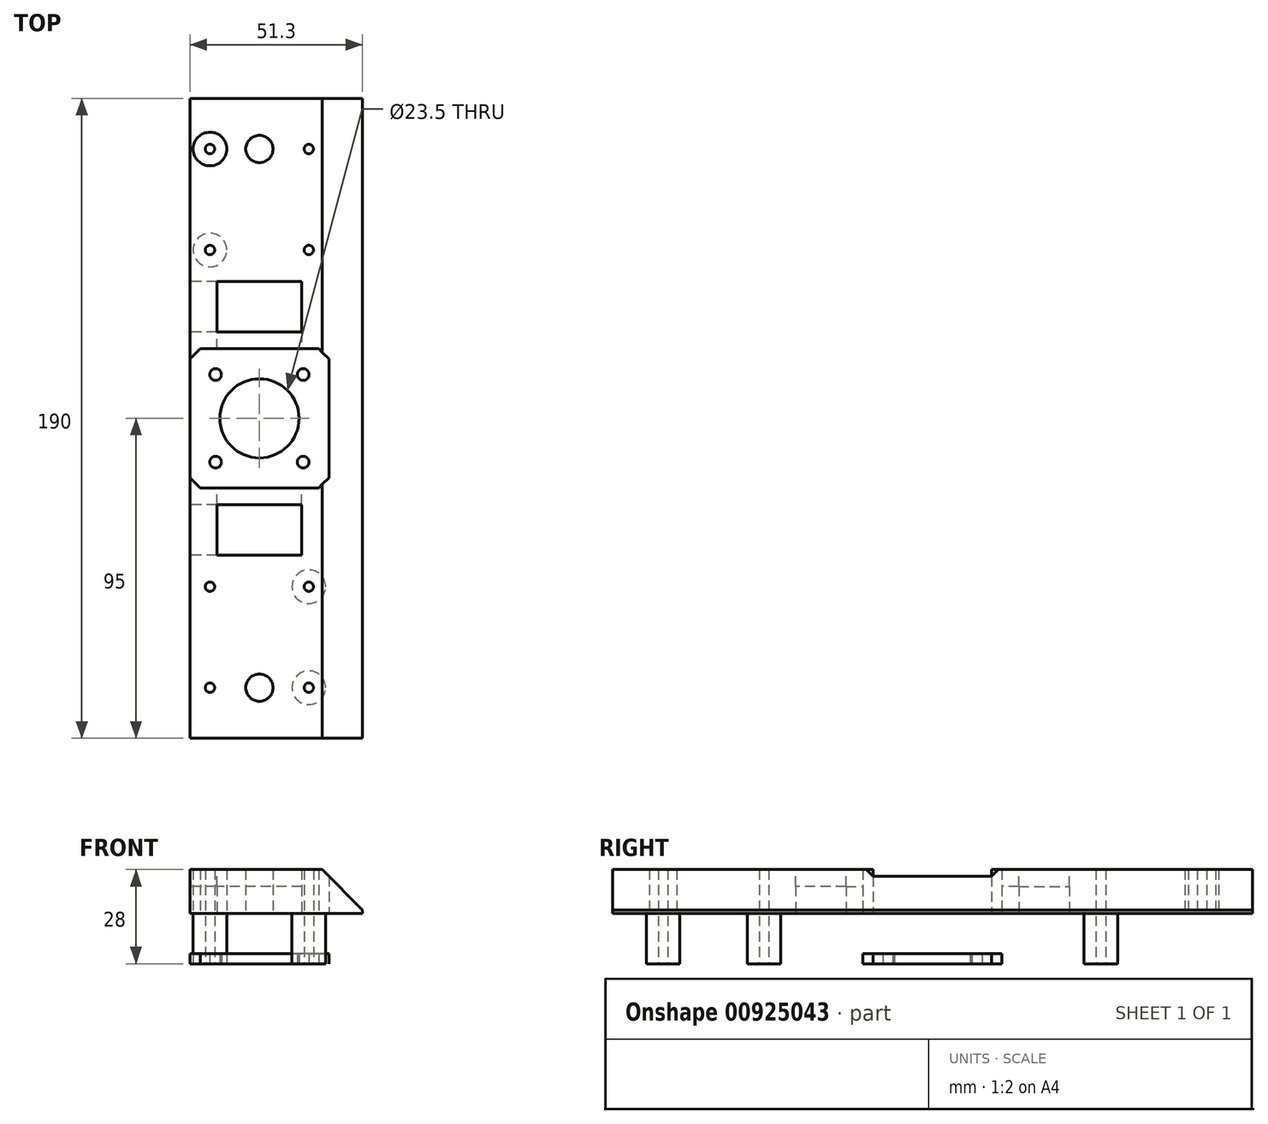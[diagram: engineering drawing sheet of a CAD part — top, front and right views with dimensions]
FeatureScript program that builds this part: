
annotation { "Feature Type Name" : "Feature", "Feature Type Description" : "" }
export const myFeature = defineFeature(function(context is Context, id is Id, definition is map)
    precondition{}
    {
        {
            var Q0;
            Q0=qCreatedBy(makeId("Top.planeOp"),FACE);
            var sketch = newSketch(context, id + "F0", { "sketchPlane" : qUnion([Q0])});
            skCircle(sketch, "E0", {"center": v(0, 0) * mm, "radius": 11.75 * mm});
            skCircle(sketch, "E1", {"center": v(13, 13) * mm, "radius": 1.75 * mm});
            skCircle(sketch, "E2.MirrorC", {"center": v(-13, -13) * mm, "radius": 1.75 * mm});
            skCircle(sketch, "E3.MirrorC", {"center": v(13, -13) * mm, "radius": 1.75 * mm});
            skLineSegment(sketch, "E4", {"start": v(-18.36, 15.65) * mm, "end": v(-15.65, 18.36) * mm});
            skLineSegment(sketch, "E5", {"start": v(-15.65, 18.36) * mm, "end": v(15.65, 18.36) * mm});
            skLineSegment(sketch, "E6", {"start": v(15.65, 18.36) * mm, "end": v(18.36, 15.65) * mm});
            skLineSegment(sketch, "E7", {"start": v(18.36, 15.65) * mm, "end": v(18.36, -15.65) * mm});
            skLineSegment(sketch, "E8", {"start": v(18.36, -15.65) * mm, "end": v(15.65, -18.36) * mm});
            skLineSegment(sketch, "E9", {"start": v(15.65, -18.36) * mm, "end": v(-15.65, -18.36) * mm});
            skLineSegment(sketch, "E10", {"start": v(-15.65, -18.36) * mm, "end": v(-18.36, -15.65) * mm});
            skLineSegment(sketch, "E11", {"start": v(-18.36, -15.65) * mm, "end": v(-18.36, 15.65) * mm});
            skCircle(sketch, "E12.MirrorC", {"center": v(-13, 13) * mm, "radius": 1.75 * mm});
            skLineSegment(sketch, "E13", {"start": v(0, 0) * mm, "end": v(-17.6, 15) * mm});
            skLineSegment(sketch, "E14", {"start": v(0, 0) * mm, "end": v(-15, 17.6) * mm});
            skLineSegment(sketch, "E15", {"start": v(0, 0) * mm, "end": v(-17.6, -15) * mm});
            skLineSegment(sketch, "E16", {"start": v(0, 0) * mm, "end": v(-15, -17.6) * mm});
            skLineSegment(sketch, "E17", {"start": v(0, 0) * mm, "end": v(15, 17.6) * mm});
            skLineSegment(sketch, "E18", {"start": v(0, 0) * mm, "end": v(17.6, 15) * mm});
            skLineSegment(sketch, "E19", {"start": v(0, 0) * mm, "end": v(15, -17.6) * mm});
            skLineSegment(sketch, "E20", {"start": v(0, 0) * mm, "end": v(17.6, -15) * mm});
            skLineSegment(sketch, "E21", {"start": v(0, 0) * mm, "end": v(15.57, 18.27) * mm});
            skLineSegment(sketch, "E22", {"start": v(0, 0) * mm, "end": v(18.27, 15.57) * mm});
            skLineSegment(sketch, "E23", {"start": v(0, 0) * mm, "end": v(18.27, -15.57) * mm});
            skLineSegment(sketch, "E24", {"start": v(0, 0) * mm, "end": v(15.57, -18.27) * mm});
            skLineSegment(sketch, "E25", {"start": v(0, 0) * mm, "end": v(-15.57, -18.27) * mm});
            skLineSegment(sketch, "E26", {"start": v(0, 0) * mm, "end": v(-18.27, -15.57) * mm});
            skLineSegment(sketch, "E27", {"start": v(0, 0) * mm, "end": v(-15.57, 18.27) * mm});
            skLineSegment(sketch, "E28", {"start": v(0, 0) * mm, "end": v(-18.27, 15.57) * mm});
            skLineSegment(sketch, "E29", {"start": v(0, 0) * mm, "end": v(17.6, 20.65) * mm});
            skLineSegment(sketch, "E30", {"start": v(17.6, 20.65) * mm, "end": v(0, 0) * mm});
            skLineSegment(sketch, "E31", {"start": v(0, 0) * mm, "end": v(20.65, 17.6) * mm});
            skLineSegment(sketch, "E32", {"start": v(0, 0) * mm, "end": v(20.65, -17.6) * mm});
            skLineSegment(sketch, "E33", {"start": v(0, 0) * mm, "end": v(17.6, -20.65) * mm});
            skLineSegment(sketch, "E34", {"start": v(0, 0) * mm, "end": v(-17.6, -20.65) * mm});
            skLineSegment(sketch, "E35", {"start": v(0, 0) * mm, "end": v(-20.65, -17.6) * mm});
            skLineSegment(sketch, "E36", {"start": v(0, 0) * mm, "end": v(-20.65, 17.6) * mm});
            skLineSegment(sketch, "E37", {"start": v(0, 0) * mm, "end": v(-17.6, 20.65) * mm});
            skLineSegment(sketch, "E38", {"start": v(17.6, 20.65) * mm, "end": v(-17.6, 20.65) * mm});
            skLineSegment(sketch, "E39", {"start": v(-17.6, 20.65) * mm, "end": v(-20.65, 17.6) * mm});
            skLineSegment(sketch, "E40", {"start": v(-20.65, 17.6) * mm, "end": v(-20.65, -17.6) * mm});
            skLineSegment(sketch, "E41", {"start": v(-20.65, -17.6) * mm, "end": v(-17.6, -20.65) * mm});
            skLineSegment(sketch, "E42", {"start": v(-17.6, -20.65) * mm, "end": v(17.6, -20.65) * mm});
            skLineSegment(sketch, "E43", {"start": v(17.6, 20.65) * mm, "end": v(20.65, 17.6) * mm});
            skLineSegment(sketch, "E44", {"start": v(20.65, 17.6) * mm, "end": v(20.65, -17.6) * mm});
            skLineSegment(sketch, "E45", {"start": v(20.65, -17.6) * mm, "end": v(17.6, -20.65) * mm});
            skLineSegment(sketch, "E46", {"start": v(20.65, 0) * mm, "end": v(30.65, 0) * mm, "construction": true});
            skLineSegment(sketch, "E47", {"start": v(30.65, 0) * mm, "end": v(30.65, -95) * mm});
            skLineSegment(sketch, "E48", {"start": v(-20.65, 0) * mm, "end": v(-20.65, -95) * mm});
            skLineSegment(sketch, "E49", {"start": v(30.65, -95) * mm, "end": v(-20.65, -95) * mm});
            skLineSegment(sketch, "E50", {"start": v(0, 0) * mm, "end": v(0, -80) * mm, "construction": true});
            skCircle(sketch, "E51", {"center": v(0, -80) * mm, "radius": 4.05 * mm});
            skLineSegment(sketch, "E52.MirrorCS", {"start": v(30.65, 0) * mm, "end": v(30.65, 95) * mm});
            skLineSegment(sketch, "E53.MirrorCS", {"start": v(-20.65, 0) * mm, "end": v(-20.65, 95) * mm});
            skLineSegment(sketch, "E54.MirrorCS", {"start": v(30.65, 95) * mm, "end": v(-20.65, 95) * mm});
            skLineSegment(sketch, "E55.MirrorCS", {"start": v(0, 0) * mm, "end": v(0, 80) * mm, "construction": true});
            skCircle(sketch, "E56.MirrorC", {"center": v(0, 80) * mm, "radius": 4.05 * mm});
            skLineSegment(sketch, "E57", {"start": v(0, -80) * mm, "end": v(-20.65, -80) * mm, "construction": true});
            skCircle(sketch, "E58", {"center": v(-14.67, -80) * mm, "radius": 1.4 * mm});
            skCircle(sketch, "E59", {"center": v(-14.67, -80) * mm, "radius": 5 * mm});
            skCircle(sketch, "E60.MirrorC", {"center": v(14.67, -80) * mm, "radius": 5 * mm});
            skCircle(sketch, "E61.MirrorC", {"center": v(14.67, -80) * mm, "radius": 1.4 * mm});
            skCircle(sketch, "E62.MirrorC", {"center": v(14.67, 80) * mm, "radius": 5 * mm});
            skCircle(sketch, "E63.MirrorC", {"center": v(14.67, 80) * mm, "radius": 1.4 * mm});
            skCircle(sketch, "E64.MirrorC", {"center": v(-14.67, 80) * mm, "radius": 1.4 * mm});
            skCircle(sketch, "E65.MirrorC", {"center": v(-14.67, 80) * mm, "radius": 5 * mm});
            skCircle(sketch, "E66.0.1.0", {"center": v(14.67, -50) * mm, "radius": 5 * mm});
            skLineSegment(sketch, "E66.direction2", {"start": v(14.67, -80) * mm, "end": v(14.67, -50) * mm, "construction": true});
            skCircle(sketch, "E67.0.1.0", {"center": v(14.67, -50) * mm, "radius": 1.4 * mm});
            skCircle(sketch, "E68.MirrorC", {"center": v(-14.67, -50) * mm, "radius": 5 * mm});
            skCircle(sketch, "E69", {"center": v(-14.67, -50) * mm, "radius": 1.4 * mm});
            skCircle(sketch, "E70.MirrorC", {"center": v(-14.67, 50) * mm, "radius": 5 * mm});
            skCircle(sketch, "E71.MirrorC", {"center": v(-14.67, 50) * mm, "radius": 1.4 * mm});
            skLineSegment(sketch, "E72", {"start": v(14.67, 80) * mm, "end": v(14.67, 50) * mm, "construction": true});
            skCircle(sketch, "E73", {"center": v(14.67, 50) * mm, "radius": 5 * mm});
            skCircle(sketch, "E74", {"center": v(14.67, 50) * mm, "radius": 1.4 * mm});
            skLineSegment(sketch, "E75", {"start": v(-14.67, 80) * mm, "end": v(-14.67, 50) * mm, "construction": true});
            skSolve(sketch);
        }
        {
            var Q0;
            Q0=makeQuery(id+"F0.imprint","IMPRINT",FACE,{"disambiguationData":[TD([[makeQuery(id+"F0.imprint","IMPRINT",EDGE,{"derivedFrom":sQuery(id+"F0.wireOp",EDGE,"E38")}),-1.0]])]});
            var Q1;
            Q1=makeQuery(id+"F0.imprint","IMPRINT",FACE,{"disambiguationData":[TD([[makeQuery(id+"F0.imprint","IMPRINT",EDGE,{"derivedFrom":sQuery(id+"F0.wireOp",EDGE,"E58")}),-1.0]])]});
            var Q2;
            Q2=makeQuery(id+"F0.imprint","IMPRINT",FACE,{"disambiguationData":[TD([[makeQuery(id+"F0.imprint","IMPRINT",EDGE,{"derivedFrom":sQuery(id+"F0.wireOp",EDGE,"E58")}),1.0]])]});
            var Q3;
            Q3=makeQuery(id+"F0.imprint","IMPRINT",FACE,{"disambiguationData":[TD([[makeQuery(id+"F0.imprint","IMPRINT",EDGE,{"derivedFrom":sQuery(id+"F0.wireOp",EDGE,"E60.MirrorC")}),-1.0]])]});
            var Q4;
            Q4=makeQuery(id+"F0.imprint","IMPRINT",FACE,{"disambiguationData":[TD([[makeQuery(id+"F0.imprint","IMPRINT",EDGE,{"derivedFrom":sQuery(id+"F0.wireOp",EDGE,"E61.MirrorC")}),-1.0]])]});
            var Q5;
            Q5=makeQuery(id+"F0.imprint","IMPRINT",FACE,{"disambiguationData":[TD([[makeQuery(id+"F0.imprint","IMPRINT",EDGE,{"derivedFrom":sQuery(id+"F0.wireOp",EDGE,"E62.MirrorC")}),1.0]])]});
            var Q6;
            Q6=makeQuery(id+"F0.imprint","IMPRINT",FACE,{"disambiguationData":[TD([[makeQuery(id+"F0.imprint","IMPRINT",EDGE,{"derivedFrom":sQuery(id+"F0.wireOp",EDGE,"E63.MirrorC")}),1.0]])]});
            var Q7;
            Q7=makeQuery(id+"F0.imprint","IMPRINT",FACE,{"disambiguationData":[TD([[makeQuery(id+"F0.imprint","IMPRINT",EDGE,{"derivedFrom":sQuery(id+"F0.wireOp",EDGE,"E64.MirrorC")}),1.0]])]});
            var Q8;
            Q8=makeQuery(id+"F0.imprint","IMPRINT",FACE,{"disambiguationData":[TD([[makeQuery(id+"F0.imprint","IMPRINT",EDGE,{"derivedFrom":sQuery(id+"F0.wireOp",EDGE,"E64.MirrorC")}),-1.0]])]});
            var Q9;
            Q9=makeQuery(id+"F0.imprint","IMPRINT",FACE,{"disambiguationData":[TD([[makeQuery(id+"F0.imprint","IMPRINT",EDGE,{"derivedFrom":sQuery(id+"F0.wireOp",EDGE,"E66.0.1.0")}),-1.0]])]});
            var Q10;
            Q10=makeQuery(id+"F0.imprint","IMPRINT",FACE,{"disambiguationData":[TD([[makeQuery(id+"F0.imprint","IMPRINT",EDGE,{"derivedFrom":sQuery(id+"F0.wireOp",EDGE,"E67.0.1.0")}),-1.0]])]});
            var Q11;
            Q11=makeQuery(id+"F0.imprint","IMPRINT",FACE,{"disambiguationData":[TD([[makeQuery(id+"F0.imprint","IMPRINT",EDGE,{"derivedFrom":sQuery(id+"F0.wireOp",EDGE,"E68.MirrorC")}),1.0]])]});
            var Q12;
            Q12=makeQuery(id+"F0.imprint","IMPRINT",FACE,{"disambiguationData":[TD([[makeQuery(id+"F0.imprint","IMPRINT",EDGE,{"derivedFrom":sQuery(id+"F0.wireOp",EDGE,"E73")}),1.0]])]});
            var Q13;
            Q13=makeQuery(id+"F0.imprint","IMPRINT",FACE,{"disambiguationData":[TD([[makeQuery(id+"F0.imprint","IMPRINT",EDGE,{"derivedFrom":sQuery(id+"F0.wireOp",EDGE,"E74")}),1.0]])]});
            var Q14;
            Q14=makeQuery(id+"F0.imprint","IMPRINT",FACE,{"disambiguationData":[TD([[makeQuery(id+"F0.imprint","IMPRINT",EDGE,{"derivedFrom":sQuery(id+"F0.wireOp",EDGE,"E70.MirrorC")}),-1.0]])]});
            var Q15;
            Q15=makeQuery(id+"F0.imprint","IMPRINT",FACE,{"disambiguationData":[TD([[makeQuery(id+"F0.imprint","IMPRINT",EDGE,{"derivedFrom":sQuery(id+"F0.wireOp",EDGE,"E71.MirrorC")}),-1.0]])]});
            var Q16;
            Q16=makeQuery(id+"F0.imprint","IMPRINT",FACE,{"disambiguationData":[TD([[makeQuery(id+"F0.imprint","IMPRINT",EDGE,{"derivedFrom":sQuery(id+"F0.wireOp",EDGE,"E69")}),1.0]])]});
            extrude(context, id + "F1", {"entities" : qUnion([Q0, Q1, Q2, Q3, Q4, Q5, Q6, Q7, Q8, Q9, Q10, Q11, Q12, Q13, Q14, Q15, Q16]), "depth" : 28 * mm, "offsetDistance" : 25 * mm});
        }
        {
            var Q0;
            {var subQ0=sQuery(id+"F0.wireOp",EDGE,"E9");Q0=makeQuery(id+"F0.imprint","IMPRINT",FACE,{"disambiguationData":[TD([[makeQuery(id+"F0.imprint","IMPRINT",EDGE,{"derivedFrom":subQ0}),1.0]])]});}
            var Q1;
            {var subQ0=sQuery(id+"F0.wireOp",EDGE,"E10");Q1=makeQuery(id+"F0.imprint","IMPRINT",FACE,{"disambiguationData":[TD([[makeQuery(id+"F0.imprint","IMPRINT",EDGE,{"derivedFrom":subQ0}),1.0]])]});}
            var Q2;
            {var subQ6=sQuery(id+"F0.wireOp",EDGE,"E11");Q2=makeQuery(id+"F0.imprint","IMPRINT",FACE,{"disambiguationData":[TD([[makeQuery(id+"F0.imprint","IMPRINT",EDGE,{"derivedFrom":subQ6}),1.0]])]});}
            var Q3;
            {var subQ0=sQuery(id+"F0.wireOp",EDGE,"E4");Q3=makeQuery(id+"F0.imprint","IMPRINT",FACE,{"disambiguationData":[TD([[makeQuery(id+"F0.imprint","IMPRINT",EDGE,{"derivedFrom":subQ0}),1.0]])]});}
            var Q4;
            {var subQ0=sQuery(id+"F0.wireOp",EDGE,"E5");Q4=makeQuery(id+"F0.imprint","IMPRINT",FACE,{"disambiguationData":[TD([[makeQuery(id+"F0.imprint","IMPRINT",EDGE,{"derivedFrom":subQ0}),1.0]])]});}
            var Q5;
            {var subQ0=sQuery(id+"F0.wireOp",EDGE,"E6");Q5=makeQuery(id+"F0.imprint","IMPRINT",FACE,{"disambiguationData":[TD([[makeQuery(id+"F0.imprint","IMPRINT",EDGE,{"derivedFrom":subQ0}),1.0]])]});}
            var Q6;
            {var subQ0=sQuery(id+"F0.wireOp",EDGE,"E7");Q6=makeQuery(id+"F0.imprint","IMPRINT",FACE,{"disambiguationData":[TD([[makeQuery(id+"F0.imprint","IMPRINT",EDGE,{"derivedFrom":subQ0}),1.0]])]});}
            var Q7;
            {var subQ0=sQuery(id+"F0.wireOp",EDGE,"E8");Q7=makeQuery(id+"F0.imprint","IMPRINT",FACE,{"disambiguationData":[TD([[makeQuery(id+"F0.imprint","IMPRINT",EDGE,{"derivedFrom":subQ0}),1.0]])]});}
            var Q8;
            {var subQ8=sQuery(id+"F0.wireOp",EDGE,"E7");Q8=makeQuery(id+"F0.imprint","IMPRINT",FACE,{"disambiguationData":[TD([[makeQuery(id+"F0.imprint","IMPRINT",EDGE,{"derivedFrom":subQ8}),-1.0]])]});}
            var Q9;
            {var subQ0=sQuery(id+"F0.wireOp",EDGE,"E33");var subQ1=sQuery(id+"F0.wireOp",EDGE,"E0");var subQ2=makeQuery(id+"F0.imprint","INTERSECT",VERTEX,{"derivedFrom":[subQ1,subQ0]});Q9=makeQuery(id+"F0.imprint","IMPRINT",FACE,{"disambiguationData":[TD([[makeQuery(id+"F0.imprint","IMPRINT",EDGE,{"disambiguationData":[TD([[subQ2,-1.0]])],"derivedFrom":subQ1}),-1.0]])]});}
            var Q10;
            {var subQ5=sQuery(id+"F0.wireOp",EDGE,"E8");Q10=makeQuery(id+"F0.imprint","IMPRINT",FACE,{"disambiguationData":[TD([[makeQuery(id+"F0.imprint","IMPRINT",EDGE,{"derivedFrom":subQ5}),-1.0]])]});}
            var Q11;
            {var subQ13=sQuery(id+"F0.wireOp",EDGE,"E9");Q11=makeQuery(id+"F0.imprint","IMPRINT",FACE,{"disambiguationData":[TD([[makeQuery(id+"F0.imprint","IMPRINT",EDGE,{"derivedFrom":subQ13}),-1.0]])]});}
            var Q12;
            {var subQ5=sQuery(id+"F0.wireOp",EDGE,"E10");Q12=makeQuery(id+"F0.imprint","IMPRINT",FACE,{"disambiguationData":[TD([[makeQuery(id+"F0.imprint","IMPRINT",EDGE,{"derivedFrom":subQ5}),-1.0]])]});}
            var Q13;
            {var subQ0=sQuery(id+"F0.wireOp",EDGE,"E35");var subQ1=sQuery(id+"F0.wireOp",EDGE,"E0");var subQ2=makeQuery(id+"F0.imprint","INTERSECT",VERTEX,{"derivedFrom":[subQ1,subQ0]});Q13=makeQuery(id+"F0.imprint","IMPRINT",FACE,{"disambiguationData":[TD([[makeQuery(id+"F0.imprint","IMPRINT",EDGE,{"disambiguationData":[TD([[subQ2,-1.0]])],"derivedFrom":subQ1}),-1.0]])]});}
            var Q14;
            {var subQ8=sQuery(id+"F0.wireOp",EDGE,"E11");Q14=makeQuery(id+"F0.imprint","IMPRINT",FACE,{"disambiguationData":[TD([[makeQuery(id+"F0.imprint","IMPRINT",EDGE,{"derivedFrom":subQ8}),-1.0]])]});}
            var Q15;
            {var subQ0=sQuery(id+"F0.wireOp",EDGE,"E37");var subQ1=sQuery(id+"F0.wireOp",EDGE,"E0");var subQ2=makeQuery(id+"F0.imprint","INTERSECT",VERTEX,{"derivedFrom":[subQ1,subQ0]});Q15=makeQuery(id+"F0.imprint","IMPRINT",FACE,{"disambiguationData":[TD([[makeQuery(id+"F0.imprint","IMPRINT",EDGE,{"disambiguationData":[TD([[subQ2,-1.0]])],"derivedFrom":subQ1}),-1.0]])]});}
            var Q16;
            {var subQ7=sQuery(id+"F0.wireOp",EDGE,"E4");Q16=makeQuery(id+"F0.imprint","IMPRINT",FACE,{"disambiguationData":[TD([[makeQuery(id+"F0.imprint","IMPRINT",EDGE,{"derivedFrom":subQ7}),-1.0]])]});}
            var Q17;
            {var subQ13=sQuery(id+"F0.wireOp",EDGE,"E5");Q17=makeQuery(id+"F0.imprint","IMPRINT",FACE,{"disambiguationData":[TD([[makeQuery(id+"F0.imprint","IMPRINT",EDGE,{"derivedFrom":subQ13}),-1.0]])]});}
            var Q18;
            {var subQ0=sQuery(id+"F0.wireOp",EDGE,"E30");var subQ1=sQuery(id+"F0.wireOp",EDGE,"E0");var subQ2=makeQuery(id+"F0.imprint","INTERSECT",VERTEX,{"derivedFrom":[subQ1,subQ0]});Q18=makeQuery(id+"F0.imprint","IMPRINT",FACE,{"disambiguationData":[TD([[makeQuery(id+"F0.imprint","IMPRINT",EDGE,{"disambiguationData":[TD([[subQ2,1.0]])],"derivedFrom":subQ1}),-1.0]])]});}
            var Q19;
            {var subQ3=sQuery(id+"F0.wireOp",EDGE,"E6");Q19=makeQuery(id+"F0.imprint","IMPRINT",FACE,{"disambiguationData":[TD([[makeQuery(id+"F0.imprint","IMPRINT",EDGE,{"derivedFrom":subQ3}),-1.0]])]});}
            extrude(context, id + "F2", {"entities" : qUnion([Q0, Q1, Q2, Q3, Q4, Q5, Q6, Q7, Q8, Q9, Q10, Q11, Q12, Q13, Q14, Q15, Q16, Q17, Q18, Q19]), "operationType" : NewBodyOperationType.ADD, "depth" : 3 * mm, "offsetDistance" : 25 * mm});
        }
        {
            var Q0;
            Q0=makeQuery(id+"F1.opExtrude","CAP_EDGE",EDGE,{"disambiguationData":[OSD([sQuery(id+"F0.wireOp",EDGE,"E47"),sQuery(id+"F0.wireOp",EDGE,"E52.MirrorCS")])],"isStart":false});
            chamfer(context, id + "F3", {"entities" : qUnion([Q0]), "width" : 12 * mm, "tangentPropagation" : true});
        }
        {
            var Q0;
            Q0=makeQuery(id+"F1.opExtrude","SWEPT_FACE",FACE,{"disambiguationData":[OSD([sQuery(id+"F0.wireOp",EDGE,"E42")])]});
            var sketch = newSketch(context, id + "F4", { "sketchPlane" : qUnion([Q0])});
            skLineSegment(sketch, "E76", {"start": v(17.6, 15.5) * mm, "end": v(12.6, 15.5) * mm});
            skLineSegment(sketch, "E77", {"start": v(0, 28) * mm, "end": v(0, 23) * mm});
            skLineSegment(sketch, "E78.bottom", {"start": v(12.6, 23) * mm, "end": v(0, 23) * mm});
            skLineSegment(sketch, "E78.top", {"start": v(12.6, 15.5) * mm, "end": v(0, 15.5) * mm});
            skLineSegment(sketch, "E78.left", {"start": v(12.6, 23) * mm, "end": v(12.6, 15.5) * mm});
            skLineSegment(sketch, "E78.right", {"start": v(0, 23) * mm, "end": v(0, 15.5) * mm});
            skLineSegment(sketch, "E79.MirrorCS", {"start": v(12.6, 8) * mm, "end": v(12.6, 15.5) * mm});
            skLineSegment(sketch, "E80.MirrorCS", {"start": v(12.6, 8) * mm, "end": v(0, 8) * mm});
            skLineSegment(sketch, "E81.MirrorCS", {"start": v(-12.6, 23) * mm, "end": v(0, 23) * mm});
            skLineSegment(sketch, "E82.MirrorCS", {"start": v(-12.6, 23) * mm, "end": v(-12.6, 15.5) * mm});
            skLineSegment(sketch, "E83.MirrorCS", {"start": v(-12.6, 8) * mm, "end": v(-12.6, 15.5) * mm});
            skLineSegment(sketch, "E84.MirrorCS", {"start": v(-12.6, 8) * mm, "end": v(0, 8) * mm});
            skSolve(sketch);
        }
        {
            var Q0;
            Q0=makeQuery(id+"F4.imprint","IMPRINT",FACE,{"disambiguationData":[TD([[makeQuery(id+"F4.imprint","IMPRINT",EDGE,{"derivedFrom":sQuery(id+"F4.wireOp",EDGE,"E78.top")}),1.0]])]});
            var Q1;
            Q1=makeQuery(id+"F4.imprint","IMPRINT",FACE,{"disambiguationData":[TD([[makeQuery(id+"F4.imprint","IMPRINT",EDGE,{"derivedFrom":sQuery(id+"F4.wireOp",EDGE,"E78.bottom")}),1.0]])]});
            extrude(context, id + "F5", {"entities" : qUnion([Q0, Q1]), "operationType" : NewBodyOperationType.REMOVE, "oppositeDirection" : true, "depth" : 20 * mm, "offsetDistance" : 25 * mm});
        }
        {
            var Q0;
            Q0=makeQuery(id+"F1.opExtrude","SWEPT_FACE",FACE,{"disambiguationData":[OSD([sQuery(id+"F0.wireOp",EDGE,"E38")])]});
            var sketch = newSketch(context, id + "F6", { "sketchPlane" : qUnion([Q0])});
            skLineSegment(sketch, "E85", {"start": v(0, 3) * mm, "end": v(0, 8) * mm});
            skLineSegment(sketch, "E86", {"start": v(-17.6, 15.5) * mm, "end": v(-12.6, 15.5) * mm});
            skLineSegment(sketch, "E87.bottom", {"start": v(-12.6, 15.5) * mm, "end": v(0, 15.5) * mm});
            skLineSegment(sketch, "E87.top", {"start": v(-12.6, 8) * mm, "end": v(0, 8) * mm});
            skLineSegment(sketch, "E87.left", {"start": v(-12.6, 15.5) * mm, "end": v(-12.6, 8) * mm});
            skLineSegment(sketch, "E87.right", {"start": v(0, 15.5) * mm, "end": v(0, 8) * mm});
            skLineSegment(sketch, "E88.MirrorCS", {"start": v(12.6, 8) * mm, "end": v(0, 8) * mm});
            skLineSegment(sketch, "E89.MirrorCS", {"start": v(12.6, 15.5) * mm, "end": v(0, 15.5) * mm});
            skLineSegment(sketch, "E90.MirrorCS", {"start": v(12.6, 15.5) * mm, "end": v(12.6, 8) * mm});
            skLineSegment(sketch, "E91.MirrorCS", {"start": v(12.6, 23) * mm, "end": v(0, 23) * mm});
            skLineSegment(sketch, "E92.MirrorCS", {"start": v(12.6, 15.5) * mm, "end": v(12.6, 23) * mm});
            skLineSegment(sketch, "E93.MirrorCS", {"start": v(-12.6, 23) * mm, "end": v(0, 23) * mm});
            skLineSegment(sketch, "E94.MirrorCS", {"start": v(-12.6, 15.5) * mm, "end": v(-12.6, 23) * mm});
            skSolve(sketch);
        }
        {
            var Q0;
            Q0=makeQuery(id+"F6.imprint","IMPRINT",FACE,{"disambiguationData":[TD([[makeQuery(id+"F6.imprint","IMPRINT",EDGE,{"derivedFrom":sQuery(id+"F6.wireOp",EDGE,"E87.right")}),1.0]])]});
            var Q1;
            Q1=makeQuery(id+"F6.imprint","IMPRINT",FACE,{"disambiguationData":[TD([[makeQuery(id+"F6.imprint","IMPRINT",EDGE,{"derivedFrom":sQuery(id+"F6.wireOp",EDGE,"E87.top")}),1.0]])]});
            var Q2;
            Q2=makeQuery(id+"F6.imprint","IMPRINT",FACE,{"disambiguationData":[TD([[makeQuery(id+"F6.imprint","IMPRINT",EDGE,{"derivedFrom":sQuery(id+"F6.wireOp",EDGE,"E89.MirrorCS")}),-1.0]])]});
            extrude(context, id + "F7", {"entities" : qUnion([Q0, Q1, Q2]), "operationType" : NewBodyOperationType.REMOVE, "oppositeDirection" : true, "depth" : 20 * mm, "offsetDistance" : 25 * mm});
        }
        {
            var Q0;
            Q0=makeQuery(id+"F3.opChamfer","SPLIT",FACE,{"disambiguationData":[OD(0.0)],"derivedFrom":makeQuery(id+"F1.opExtrude","CAP_FACE",FACE,{"disambiguationData":[OSD([sQuery(id+"F0.wireOp",EDGE,"E38"),sQuery(id+"F0.wireOp",EDGE,"E39"),sQuery(id+"F0.wireOp",EDGE,"E41"),sQuery(id+"F0.wireOp",EDGE,"E42"),sQuery(id+"F0.wireOp",EDGE,"E43"),sQuery(id+"F0.wireOp",EDGE,"E44"),sQuery(id+"F0.wireOp",EDGE,"E45"),sQuery(id+"F0.wireOp",EDGE,"E47"),sQuery(id+"F0.wireOp",EDGE,"E48"),sQuery(id+"F0.wireOp",EDGE,"E49"),sQuery(id+"F0.wireOp",EDGE,"E51"),sQuery(id+"F0.wireOp",EDGE,"E52.MirrorCS"),sQuery(id+"F0.wireOp",EDGE,"E53.MirrorCS"),sQuery(id+"F0.wireOp",EDGE,"E54.MirrorCS"),sQuery(id+"F0.wireOp",EDGE,"E56.MirrorC")])],"isStart":false})});
            var sketch = newSketch(context, id + "F8", { "sketchPlane" : qUnion([Q0])});
            skLineSegment(sketch, "E95", {"start": v(0, 20.65) * mm, "end": v(0, 40.65) * mm, "construction": true});
            skLineSegment(sketch, "E96.bottom", {"start": v(0, 40.65) * mm, "end": v(12.59, 40.65) * mm});
            skLineSegment(sketch, "E96.top", {"start": v(0, 25.65) * mm, "end": v(12.59, 25.65) * mm});
            skLineSegment(sketch, "E96.left", {"start": v(0, 40.65) * mm, "end": v(0, 25.65) * mm});
            skLineSegment(sketch, "E96.right", {"start": v(12.59, 40.65) * mm, "end": v(12.59, 25.65) * mm});
            skLineSegment(sketch, "E97.MirrorCS", {"start": v(0, 40.65) * mm, "end": v(-12.6, 40.65) * mm});
            skLineSegment(sketch, "E98.MirrorCS", {"start": v(-12.6, 40.65) * mm, "end": v(-12.6, 25.65) * mm});
            skLineSegment(sketch, "E99.MirrorCS", {"start": v(0, 25.65) * mm, "end": v(-12.6, 25.65) * mm});
            skLineSegment(sketch, "E100", {"start": v(-12.6, 25.65) * mm, "end": v(-20.65, 25.65) * mm, "construction": true});
            skSolve(sketch);
        }
        {
            var Q0;
            Q0=makeQuery(id+"F8.imprint","IMPRINT",FACE,{"disambiguationData":[TD([[makeQuery(id+"F8.imprint","IMPRINT",EDGE,{"derivedFrom":sQuery(id+"F8.wireOp",EDGE,"E96.bottom")}),-1.0]])]});
            var Q1;
            Q1=makeQuery(id+"F8.imprint","IMPRINT",FACE,{"disambiguationData":[TD([[makeQuery(id+"F8.imprint","IMPRINT",EDGE,{"derivedFrom":sQuery(id+"F8.wireOp",EDGE,"E96.left")}),-1.0]])]});
            extrude(context, id + "F9", {"entities" : qUnion([Q0, Q1]), "operationType" : NewBodyOperationType.REMOVE, "oppositeDirection" : true, "depth" : 28 * mm, "offsetDistance" : 25 * mm});
        }
        {
            var Q0;
            {var subQ0=sQuery(id+"F0.wireOp",EDGE,"E53.MirrorCS");var subQ1=sQuery(id+"F0.wireOp",EDGE,"E48");Q0=makeQuery(id+"F2.boolean.opBoolean","MERGE",FACE,{"derivedFrom":[makeQuery(id+"F1.opExtrude","SWEPT_FACE",FACE,{"disambiguationData":[OSD([subQ1])]}),makeQuery(id+"F1.opExtrude","SWEPT_FACE",FACE,{"disambiguationData":[OSD([subQ0])]}),makeQuery(id+"F2.opExtrude","SWEPT_FACE",FACE,{"disambiguationData":[OSD([subQ1,subQ0])]})]});}
            var sketch = newSketch(context, id + "F10", { "sketchPlane" : qUnion([Q0])});
            skLineSegment(sketch, "E101", {"start": v(-25.65, 28) * mm, "end": v(-25.65, 23) * mm});
            skLineSegment(sketch, "E102.bottom", {"start": v(-25.65, 23) * mm, "end": v(-40.65, 23) * mm});
            skLineSegment(sketch, "E102.top", {"start": v(-25.65, 3) * mm, "end": v(-40.65, 3) * mm});
            skLineSegment(sketch, "E102.left", {"start": v(-25.65, 23) * mm, "end": v(-25.65, 3) * mm});
            skLineSegment(sketch, "E102.right", {"start": v(-40.65, 23) * mm, "end": v(-40.65, 3) * mm});
            skLineSegment(sketch, "E103.MirrorCS", {"start": v(25.65, 3) * mm, "end": v(40.65, 3) * mm});
            skLineSegment(sketch, "E104.MirrorCS", {"start": v(40.65, 23) * mm, "end": v(40.65, 3) * mm});
            skLineSegment(sketch, "E105.MirrorCS", {"start": v(25.65, 23) * mm, "end": v(40.65, 23) * mm});
            skLineSegment(sketch, "E106.MirrorCS", {"start": v(25.65, 23) * mm, "end": v(25.65, 3) * mm});
            skSolve(sketch);
        }
        {
            var Q0;
            Q0=makeQuery(id+"F10.imprint","IMPRINT",FACE,{"disambiguationData":[TD([[makeQuery(id+"F10.imprint","IMPRINT",EDGE,{"derivedFrom":sQuery(id+"F10.wireOp",EDGE,"E102.bottom")}),1.0]])]});
            extrude(context, id + "F11", {"entities" : qUnion([Q0]), "operationType" : NewBodyOperationType.REMOVE, "oppositeDirection" : true, "depth" : 25 * mm, "offsetDistance" : 25 * mm});
        }
        {
            var Q0;
            Q0=makeQuery(id+"F3.opChamfer","SPLIT",FACE,{"disambiguationData":[OD(1.0)],"derivedFrom":makeQuery(id+"F1.opExtrude","CAP_FACE",FACE,{"disambiguationData":[OSD([sQuery(id+"F0.wireOp",EDGE,"E38"),sQuery(id+"F0.wireOp",EDGE,"E39"),sQuery(id+"F0.wireOp",EDGE,"E41"),sQuery(id+"F0.wireOp",EDGE,"E42"),sQuery(id+"F0.wireOp",EDGE,"E43"),sQuery(id+"F0.wireOp",EDGE,"E44"),sQuery(id+"F0.wireOp",EDGE,"E45"),sQuery(id+"F0.wireOp",EDGE,"E47"),sQuery(id+"F0.wireOp",EDGE,"E48"),sQuery(id+"F0.wireOp",EDGE,"E49"),sQuery(id+"F0.wireOp",EDGE,"E51"),sQuery(id+"F0.wireOp",EDGE,"E52.MirrorCS"),sQuery(id+"F0.wireOp",EDGE,"E53.MirrorCS"),sQuery(id+"F0.wireOp",EDGE,"E54.MirrorCS"),sQuery(id+"F0.wireOp",EDGE,"E56.MirrorC")])],"isStart":false})});
            var sketch = newSketch(context, id + "F12", { "sketchPlane" : qUnion([Q0])});
            skLineSegment(sketch, "E107", {"start": v(0, -20.65) * mm, "end": v(0, -40.65) * mm, "construction": true});
            skLineSegment(sketch, "E108.bottom", {"start": v(0, -40.65) * mm, "end": v(-12.59, -40.65) * mm});
            skLineSegment(sketch, "E108.top", {"start": v(0, -25.65) * mm, "end": v(-12.59, -25.65) * mm});
            skLineSegment(sketch, "E108.left", {"start": v(1.85, 8.61) * mm, "end": v(1.85, -6.39) * mm});
            skLineSegment(sketch, "E108.right", {"start": v(-12.59, -40.65) * mm, "end": v(-12.59, -25.65) * mm});
            skLineSegment(sketch, "E109.MirrorCS", {"start": v(0, -40.65) * mm, "end": v(12.6, -40.65) * mm});
            skLineSegment(sketch, "E110.MirrorCS", {"start": v(12.6, -40.65) * mm, "end": v(12.6, -25.65) * mm});
            skLineSegment(sketch, "E111.MirrorCS", {"start": v(0, -25.65) * mm, "end": v(12.6, -25.65) * mm});
            skLineSegment(sketch, "E112", {"start": v(-10.74, -6.39) * mm, "end": v(-18.8, -6.39) * mm, "construction": true});
            skSolve(sketch);
        }
        {
            var Q0;
            Q0=makeQuery(id+"F12.imprint","IMPRINT",FACE,{"disambiguationData":[TD([[makeQuery(id+"F12.imprint","IMPRINT",EDGE,{"derivedFrom":sQuery(id+"F12.wireOp",EDGE,"E108.bottom")}),-1.0]])]});
            extrude(context, id + "F13", {"entities" : qUnion([Q0]), "operationType" : NewBodyOperationType.REMOVE, "oppositeDirection" : true, "depth" : 28 * mm, "offsetDistance" : 25 * mm});
        }
        {
            var Q0;
            Q0=makeQuery(id+"F10.imprint","IMPRINT",FACE,{"disambiguationData":[TD([[makeQuery(id+"F10.imprint","IMPRINT",EDGE,{"derivedFrom":sQuery(id+"F10.wireOp",EDGE,"E103.MirrorCS")}),1.0]])]});
            extrude(context, id + "F14", {"entities" : qUnion([Q0]), "operationType" : NewBodyOperationType.REMOVE, "oppositeDirection" : true, "depth" : 25 * mm, "offsetDistance" : 25 * mm});
        }
        {
            var Q0;
            Q0=makeQuery(id+"F0.imprint","IMPRINT",FACE,{"disambiguationData":[TD([[makeQuery(id+"F0.imprint","IMPRINT",EDGE,{"derivedFrom":sQuery(id+"F0.wireOp",EDGE,"E60.MirrorC")}),-1.0]])]});
            var Q1;
            Q1=makeQuery(id+"F0.imprint","IMPRINT",FACE,{"disambiguationData":[TD([[makeQuery(id+"F0.imprint","IMPRINT",EDGE,{"derivedFrom":sQuery(id+"F0.wireOp",EDGE,"E58")}),-1.0]])]});
            var Q2;
            Q2=makeQuery(id+"F0.imprint","IMPRINT",FACE,{"disambiguationData":[TD([[makeQuery(id+"F0.imprint","IMPRINT",EDGE,{"derivedFrom":sQuery(id+"F0.wireOp",EDGE,"E68.MirrorC")}),1.0]])]});
            var Q3;
            Q3=makeQuery(id+"F0.imprint","IMPRINT",FACE,{"disambiguationData":[TD([[makeQuery(id+"F0.imprint","IMPRINT",EDGE,{"derivedFrom":sQuery(id+"F0.wireOp",EDGE,"E66.0.1.0")}),-1.0]])]});
            var Q4;
            Q4=makeQuery(id+"F0.imprint","IMPRINT",FACE,{"disambiguationData":[TD([[makeQuery(id+"F0.imprint","IMPRINT",EDGE,{"derivedFrom":sQuery(id+"F0.wireOp",EDGE,"E62.MirrorC")}),1.0]])]});
            var Q5;
            Q5=makeQuery(id+"F0.imprint","IMPRINT",FACE,{"disambiguationData":[TD([[makeQuery(id+"F0.imprint","IMPRINT",EDGE,{"derivedFrom":sQuery(id+"F0.wireOp",EDGE,"E73")}),1.0]])]});
            var Q6;
            Q6=makeQuery(id+"F0.imprint","IMPRINT",FACE,{"disambiguationData":[TD([[makeQuery(id+"F0.imprint","IMPRINT",EDGE,{"derivedFrom":sQuery(id+"F0.wireOp",EDGE,"E64.MirrorC")}),1.0]])]});
            var Q7;
            Q7=makeQuery(id+"F0.imprint","IMPRINT",FACE,{"disambiguationData":[TD([[makeQuery(id+"F0.imprint","IMPRINT",EDGE,{"derivedFrom":sQuery(id+"F0.wireOp",EDGE,"E70.MirrorC")}),-1.0]])]});
            extrude(context, id + "F15", {"entities" : qUnion([Q0, Q1, Q2, Q3, Q4, Q5, Q6, Q7]), "operationType" : NewBodyOperationType.REMOVE, "oppositeDirection" : true, "depth" : -15 * mm, "offsetDistance" : 25 * mm});
        }
        {
            var Q0;
            {var subQ0=sQuery(id+"F0.wireOp",EDGE,"E53.MirrorCS");var subQ1=sQuery(id+"F0.wireOp",EDGE,"E48");var subQ2=sQuery(id+"F0.wireOp",EDGE,"E45");var subQ3=sQuery(id+"F0.wireOp",EDGE,"E44");var subQ4=sQuery(id+"F0.wireOp",EDGE,"E43");var subQ5=sQuery(id+"F0.wireOp",EDGE,"E42");var subQ6=sQuery(id+"F0.wireOp",EDGE,"E41");var subQ7=sQuery(id+"F0.wireOp",EDGE,"E39");var subQ8=sQuery(id+"F0.wireOp",EDGE,"E38");Q0=makeQuery(id+"F15.boolean.opBoolean","SPLIT",FACE,{"disambiguationData":[TD([makeQuery(id+"F15.opExtrude","SWEPT_FACE",FACE,{"disambiguationData":[OSD([sQuery(id+"F0.wireOp",EDGE,"E63.MirrorC")])]})])],"derivedFrom":makeQuery(id+"F2.boolean.opBoolean","MERGE",FACE,{"derivedFrom":[makeQuery(id+"F1.opExtrude","CAP_FACE",FACE,{"disambiguationData":[OSD([subQ8,subQ7,subQ6,subQ5,subQ4,subQ3,subQ2,sQuery(id+"F0.wireOp",EDGE,"E47"),subQ1,sQuery(id+"F0.wireOp",EDGE,"E49"),sQuery(id+"F0.wireOp",EDGE,"E51"),sQuery(id+"F0.wireOp",EDGE,"E52.MirrorCS"),subQ0,sQuery(id+"F0.wireOp",EDGE,"E54.MirrorCS"),sQuery(id+"F0.wireOp",EDGE,"E56.MirrorC")])],"isStart":true}),makeQuery(id+"F2.opExtrude","CAP_FACE",FACE,{"disambiguationData":[OSD([sQuery(id+"F0.wireOp",EDGE,"E0"),sQuery(id+"F0.wireOp",EDGE,"E1"),sQuery(id+"F0.wireOp",EDGE,"E2.MirrorC"),sQuery(id+"F0.wireOp",EDGE,"E3.MirrorC"),sQuery(id+"F0.wireOp",EDGE,"E12.MirrorC"),subQ8,subQ7,subQ6,subQ5,subQ4,subQ3,subQ2,subQ1,subQ0])],"isStart":true})]})});}
            var Q1;
            {var subQ0=sQuery(id+"F0.wireOp",EDGE,"E53.MirrorCS");var subQ1=sQuery(id+"F0.wireOp",EDGE,"E48");var subQ2=sQuery(id+"F0.wireOp",EDGE,"E45");var subQ3=sQuery(id+"F0.wireOp",EDGE,"E44");var subQ4=sQuery(id+"F0.wireOp",EDGE,"E43");var subQ5=sQuery(id+"F0.wireOp",EDGE,"E42");var subQ6=sQuery(id+"F0.wireOp",EDGE,"E41");var subQ7=sQuery(id+"F0.wireOp",EDGE,"E39");var subQ8=sQuery(id+"F0.wireOp",EDGE,"E38");Q1=makeQuery(id+"F15.boolean.opBoolean","SPLIT",FACE,{"disambiguationData":[TD([makeQuery(id+"F15.opExtrude","SWEPT_FACE",FACE,{"disambiguationData":[OSD([sQuery(id+"F0.wireOp",EDGE,"E71.MirrorC")])]})])],"derivedFrom":makeQuery(id+"F2.boolean.opBoolean","MERGE",FACE,{"derivedFrom":[makeQuery(id+"F1.opExtrude","CAP_FACE",FACE,{"disambiguationData":[OSD([subQ8,subQ7,subQ6,subQ5,subQ4,subQ3,subQ2,sQuery(id+"F0.wireOp",EDGE,"E47"),subQ1,sQuery(id+"F0.wireOp",EDGE,"E49"),sQuery(id+"F0.wireOp",EDGE,"E51"),sQuery(id+"F0.wireOp",EDGE,"E52.MirrorCS"),subQ0,sQuery(id+"F0.wireOp",EDGE,"E54.MirrorCS"),sQuery(id+"F0.wireOp",EDGE,"E56.MirrorC")])],"isStart":true}),makeQuery(id+"F2.opExtrude","CAP_FACE",FACE,{"disambiguationData":[OSD([sQuery(id+"F0.wireOp",EDGE,"E0"),sQuery(id+"F0.wireOp",EDGE,"E1"),sQuery(id+"F0.wireOp",EDGE,"E2.MirrorC"),sQuery(id+"F0.wireOp",EDGE,"E3.MirrorC"),sQuery(id+"F0.wireOp",EDGE,"E12.MirrorC"),subQ8,subQ7,subQ6,subQ5,subQ4,subQ3,subQ2,subQ1,subQ0])],"isStart":true})]})});}
            var Q2;
            {var subQ0=sQuery(id+"F0.wireOp",EDGE,"E53.MirrorCS");var subQ1=sQuery(id+"F0.wireOp",EDGE,"E48");var subQ2=sQuery(id+"F0.wireOp",EDGE,"E45");var subQ3=sQuery(id+"F0.wireOp",EDGE,"E44");var subQ4=sQuery(id+"F0.wireOp",EDGE,"E43");var subQ5=sQuery(id+"F0.wireOp",EDGE,"E42");var subQ6=sQuery(id+"F0.wireOp",EDGE,"E41");var subQ7=sQuery(id+"F0.wireOp",EDGE,"E39");var subQ8=sQuery(id+"F0.wireOp",EDGE,"E38");Q2=makeQuery(id+"F15.boolean.opBoolean","SPLIT",FACE,{"disambiguationData":[TD([makeQuery(id+"F15.opExtrude","SWEPT_FACE",FACE,{"disambiguationData":[OSD([sQuery(id+"F0.wireOp",EDGE,"E74")])]})])],"derivedFrom":makeQuery(id+"F2.boolean.opBoolean","MERGE",FACE,{"derivedFrom":[makeQuery(id+"F1.opExtrude","CAP_FACE",FACE,{"disambiguationData":[OSD([subQ8,subQ7,subQ6,subQ5,subQ4,subQ3,subQ2,sQuery(id+"F0.wireOp",EDGE,"E47"),subQ1,sQuery(id+"F0.wireOp",EDGE,"E49"),sQuery(id+"F0.wireOp",EDGE,"E51"),sQuery(id+"F0.wireOp",EDGE,"E52.MirrorCS"),subQ0,sQuery(id+"F0.wireOp",EDGE,"E54.MirrorCS"),sQuery(id+"F0.wireOp",EDGE,"E56.MirrorC")])],"isStart":true}),makeQuery(id+"F2.opExtrude","CAP_FACE",FACE,{"disambiguationData":[OSD([sQuery(id+"F0.wireOp",EDGE,"E0"),sQuery(id+"F0.wireOp",EDGE,"E1"),sQuery(id+"F0.wireOp",EDGE,"E2.MirrorC"),sQuery(id+"F0.wireOp",EDGE,"E3.MirrorC"),sQuery(id+"F0.wireOp",EDGE,"E12.MirrorC"),subQ8,subQ7,subQ6,subQ5,subQ4,subQ3,subQ2,subQ1,subQ0])],"isStart":true})]})});}
            var Q3;
            {var subQ0=sQuery(id+"F0.wireOp",EDGE,"E53.MirrorCS");var subQ1=sQuery(id+"F0.wireOp",EDGE,"E48");var subQ2=sQuery(id+"F0.wireOp",EDGE,"E45");var subQ3=sQuery(id+"F0.wireOp",EDGE,"E44");var subQ4=sQuery(id+"F0.wireOp",EDGE,"E43");var subQ5=sQuery(id+"F0.wireOp",EDGE,"E42");var subQ6=sQuery(id+"F0.wireOp",EDGE,"E41");var subQ7=sQuery(id+"F0.wireOp",EDGE,"E39");var subQ8=sQuery(id+"F0.wireOp",EDGE,"E38");Q3=makeQuery(id+"F15.boolean.opBoolean","SPLIT",FACE,{"disambiguationData":[TD([makeQuery(id+"F15.opExtrude","SWEPT_FACE",FACE,{"disambiguationData":[OSD([sQuery(id+"F0.wireOp",EDGE,"E67.0.1.0")])]})])],"derivedFrom":makeQuery(id+"F2.boolean.opBoolean","MERGE",FACE,{"derivedFrom":[makeQuery(id+"F1.opExtrude","CAP_FACE",FACE,{"disambiguationData":[OSD([subQ8,subQ7,subQ6,subQ5,subQ4,subQ3,subQ2,sQuery(id+"F0.wireOp",EDGE,"E47"),subQ1,sQuery(id+"F0.wireOp",EDGE,"E49"),sQuery(id+"F0.wireOp",EDGE,"E51"),sQuery(id+"F0.wireOp",EDGE,"E52.MirrorCS"),subQ0,sQuery(id+"F0.wireOp",EDGE,"E54.MirrorCS"),sQuery(id+"F0.wireOp",EDGE,"E56.MirrorC")])],"isStart":true}),makeQuery(id+"F2.opExtrude","CAP_FACE",FACE,{"disambiguationData":[OSD([sQuery(id+"F0.wireOp",EDGE,"E0"),sQuery(id+"F0.wireOp",EDGE,"E1"),sQuery(id+"F0.wireOp",EDGE,"E2.MirrorC"),sQuery(id+"F0.wireOp",EDGE,"E3.MirrorC"),sQuery(id+"F0.wireOp",EDGE,"E12.MirrorC"),subQ8,subQ7,subQ6,subQ5,subQ4,subQ3,subQ2,subQ1,subQ0])],"isStart":true})]})});}
            var Q4;
            {var subQ0=sQuery(id+"F0.wireOp",EDGE,"E53.MirrorCS");var subQ1=sQuery(id+"F0.wireOp",EDGE,"E48");var subQ2=sQuery(id+"F0.wireOp",EDGE,"E45");var subQ3=sQuery(id+"F0.wireOp",EDGE,"E44");var subQ4=sQuery(id+"F0.wireOp",EDGE,"E43");var subQ5=sQuery(id+"F0.wireOp",EDGE,"E42");var subQ6=sQuery(id+"F0.wireOp",EDGE,"E41");var subQ7=sQuery(id+"F0.wireOp",EDGE,"E39");var subQ8=sQuery(id+"F0.wireOp",EDGE,"E38");Q4=makeQuery(id+"F15.boolean.opBoolean","SPLIT",FACE,{"disambiguationData":[TD([makeQuery(id+"F15.opExtrude","SWEPT_FACE",FACE,{"disambiguationData":[OSD([sQuery(id+"F0.wireOp",EDGE,"E69")])]})])],"derivedFrom":makeQuery(id+"F2.boolean.opBoolean","MERGE",FACE,{"derivedFrom":[makeQuery(id+"F1.opExtrude","CAP_FACE",FACE,{"disambiguationData":[OSD([subQ8,subQ7,subQ6,subQ5,subQ4,subQ3,subQ2,sQuery(id+"F0.wireOp",EDGE,"E47"),subQ1,sQuery(id+"F0.wireOp",EDGE,"E49"),sQuery(id+"F0.wireOp",EDGE,"E51"),sQuery(id+"F0.wireOp",EDGE,"E52.MirrorCS"),subQ0,sQuery(id+"F0.wireOp",EDGE,"E54.MirrorCS"),sQuery(id+"F0.wireOp",EDGE,"E56.MirrorC")])],"isStart":true}),makeQuery(id+"F2.opExtrude","CAP_FACE",FACE,{"disambiguationData":[OSD([sQuery(id+"F0.wireOp",EDGE,"E0"),sQuery(id+"F0.wireOp",EDGE,"E1"),sQuery(id+"F0.wireOp",EDGE,"E2.MirrorC"),sQuery(id+"F0.wireOp",EDGE,"E3.MirrorC"),sQuery(id+"F0.wireOp",EDGE,"E12.MirrorC"),subQ8,subQ7,subQ6,subQ5,subQ4,subQ3,subQ2,subQ1,subQ0])],"isStart":true})]})});}
            var Q5;
            {var subQ0=sQuery(id+"F0.wireOp",EDGE,"E53.MirrorCS");var subQ1=sQuery(id+"F0.wireOp",EDGE,"E48");var subQ2=sQuery(id+"F0.wireOp",EDGE,"E45");var subQ3=sQuery(id+"F0.wireOp",EDGE,"E44");var subQ4=sQuery(id+"F0.wireOp",EDGE,"E43");var subQ5=sQuery(id+"F0.wireOp",EDGE,"E42");var subQ6=sQuery(id+"F0.wireOp",EDGE,"E41");var subQ7=sQuery(id+"F0.wireOp",EDGE,"E39");var subQ8=sQuery(id+"F0.wireOp",EDGE,"E38");Q5=makeQuery(id+"F15.boolean.opBoolean","SPLIT",FACE,{"disambiguationData":[TD([makeQuery(id+"F15.opExtrude","SWEPT_FACE",FACE,{"disambiguationData":[OSD([sQuery(id+"F0.wireOp",EDGE,"E61.MirrorC")])]})])],"derivedFrom":makeQuery(id+"F2.boolean.opBoolean","MERGE",FACE,{"derivedFrom":[makeQuery(id+"F1.opExtrude","CAP_FACE",FACE,{"disambiguationData":[OSD([subQ8,subQ7,subQ6,subQ5,subQ4,subQ3,subQ2,sQuery(id+"F0.wireOp",EDGE,"E47"),subQ1,sQuery(id+"F0.wireOp",EDGE,"E49"),sQuery(id+"F0.wireOp",EDGE,"E51"),sQuery(id+"F0.wireOp",EDGE,"E52.MirrorCS"),subQ0,sQuery(id+"F0.wireOp",EDGE,"E54.MirrorCS"),sQuery(id+"F0.wireOp",EDGE,"E56.MirrorC")])],"isStart":true}),makeQuery(id+"F2.opExtrude","CAP_FACE",FACE,{"disambiguationData":[OSD([sQuery(id+"F0.wireOp",EDGE,"E0"),sQuery(id+"F0.wireOp",EDGE,"E1"),sQuery(id+"F0.wireOp",EDGE,"E2.MirrorC"),sQuery(id+"F0.wireOp",EDGE,"E3.MirrorC"),sQuery(id+"F0.wireOp",EDGE,"E12.MirrorC"),subQ8,subQ7,subQ6,subQ5,subQ4,subQ3,subQ2,subQ1,subQ0])],"isStart":true})]})});}
            var Q6;
            {var subQ0=sQuery(id+"F0.wireOp",EDGE,"E53.MirrorCS");var subQ1=sQuery(id+"F0.wireOp",EDGE,"E48");var subQ2=sQuery(id+"F0.wireOp",EDGE,"E45");var subQ3=sQuery(id+"F0.wireOp",EDGE,"E44");var subQ4=sQuery(id+"F0.wireOp",EDGE,"E43");var subQ5=sQuery(id+"F0.wireOp",EDGE,"E42");var subQ6=sQuery(id+"F0.wireOp",EDGE,"E41");var subQ7=sQuery(id+"F0.wireOp",EDGE,"E39");var subQ8=sQuery(id+"F0.wireOp",EDGE,"E38");Q6=makeQuery(id+"F15.boolean.opBoolean","SPLIT",FACE,{"disambiguationData":[TD([makeQuery(id+"F15.opExtrude","SWEPT_FACE",FACE,{"disambiguationData":[OSD([sQuery(id+"F0.wireOp",EDGE,"E58")])]})])],"derivedFrom":makeQuery(id+"F2.boolean.opBoolean","MERGE",FACE,{"derivedFrom":[makeQuery(id+"F1.opExtrude","CAP_FACE",FACE,{"disambiguationData":[OSD([subQ8,subQ7,subQ6,subQ5,subQ4,subQ3,subQ2,sQuery(id+"F0.wireOp",EDGE,"E47"),subQ1,sQuery(id+"F0.wireOp",EDGE,"E49"),sQuery(id+"F0.wireOp",EDGE,"E51"),sQuery(id+"F0.wireOp",EDGE,"E52.MirrorCS"),subQ0,sQuery(id+"F0.wireOp",EDGE,"E54.MirrorCS"),sQuery(id+"F0.wireOp",EDGE,"E56.MirrorC")])],"isStart":true}),makeQuery(id+"F2.opExtrude","CAP_FACE",FACE,{"disambiguationData":[OSD([sQuery(id+"F0.wireOp",EDGE,"E0"),sQuery(id+"F0.wireOp",EDGE,"E1"),sQuery(id+"F0.wireOp",EDGE,"E2.MirrorC"),sQuery(id+"F0.wireOp",EDGE,"E3.MirrorC"),sQuery(id+"F0.wireOp",EDGE,"E12.MirrorC"),subQ8,subQ7,subQ6,subQ5,subQ4,subQ3,subQ2,subQ1,subQ0])],"isStart":true})]})});}
            var Q7;
            Q7=makeQuery(id+"F0.imprint","IMPRINT",FACE,{"disambiguationData":[TD([[makeQuery(id+"F0.imprint","IMPRINT",EDGE,{"derivedFrom":sQuery(id+"F0.wireOp",EDGE,"E64.MirrorC")}),-1.0]])]});
            extrude(context, id + "F16", {"entities" : qUnion([Q0, Q1, Q2, Q3, Q4, Q5, Q6, Q7]), "operationType" : NewBodyOperationType.REMOVE, "oppositeDirection" : true, "depth" : 28 * mm, "offsetDistance" : 25 * mm});
        }
        {
            var Q0;
            {var subQ0=sQuery(id+"F0.wireOp",EDGE,"E53.MirrorCS");var subQ1=sQuery(id+"F0.wireOp",EDGE,"E48");Q0=makeQuery(id+"F2.boolean.opBoolean","MERGE",FACE,{"derivedFrom":[makeQuery(id+"F1.opExtrude","SWEPT_FACE",FACE,{"disambiguationData":[OSD([subQ1])]}),makeQuery(id+"F1.opExtrude","SWEPT_FACE",FACE,{"disambiguationData":[OSD([subQ0])]}),makeQuery(id+"F2.opExtrude","SWEPT_FACE",FACE,{"disambiguationData":[OSD([subQ1,subQ0])]})]});}
            var sketch = newSketch(context, id + "F17", { "sketchPlane" : qUnion([Q0])});
            skLineSegment(sketch, "E113", {"start": v(80, 0) * mm, "end": v(80, 28) * mm, "construction": true});
            skCircle(sketch, "E114", {"center": v(65, 8) * mm, "radius": 5 * mm});
            skCircle(sketch, "E115", {"center": v(65, 8) * mm, "radius": 1.4 * mm});
            skCircle(sketch, "E116", {"center": v(33.15, 8) * mm, "radius": 5 * mm});
            skCircle(sketch, "E117", {"center": v(33.15, 8) * mm, "radius": 1.4 * mm});
            skCircle(sketch, "E118.MirrorC", {"center": v(-33.15, 8) * mm, "radius": 5 * mm});
            skCircle(sketch, "E119.MirrorC", {"center": v(-33.15, 8) * mm, "radius": 1.4 * mm});
            skCircle(sketch, "E120.MirrorC", {"center": v(-65, 8) * mm, "radius": 5 * mm});
            skCircle(sketch, "E121.MirrorC", {"center": v(-65, 8) * mm, "radius": 1.4 * mm});
            skCircle(sketch, "E122", {"center": v(0, 8) * mm, "radius": 5 * mm});
            skCircle(sketch, "E123", {"center": v(0, 8) * mm, "radius": 1.4 * mm});
            skLineSegment(sketch, "E124", {"start": v(65, 0) * mm, "end": v(65, 8) * mm, "construction": true});
            skLineSegment(sketch, "E125", {"start": v(65, 8) * mm, "end": v(-95, 8) * mm, "construction": true});
            skLineSegment(sketch, "E126", {"start": v(33.15, 3) * mm, "end": v(33.15, 0) * mm, "construction": true});
            skSolve(sketch);
        }
        {
            var Q0;
            Q0=makeQuery(id+"F17.imprint","IMPRINT",FACE,{"disambiguationData":[TD([[makeQuery(id+"F17.imprint","IMPRINT",EDGE,{"derivedFrom":sQuery(id+"F17.wireOp",EDGE,"E114")}),1.0]])]});
            var Q1;
            Q1=makeQuery(id+"F17.imprint","IMPRINT",FACE,{"disambiguationData":[TD([[makeQuery(id+"F17.imprint","IMPRINT",EDGE,{"derivedFrom":sQuery(id+"F17.wireOp",EDGE,"E116")}),1.0]])]});
            var Q2;
            Q2=makeQuery(id+"F17.imprint","IMPRINT",FACE,{"disambiguationData":[TD([[makeQuery(id+"F17.imprint","IMPRINT",EDGE,{"derivedFrom":sQuery(id+"F17.wireOp",EDGE,"E122")}),1.0]])]});
            var Q3;
            Q3=makeQuery(id+"F17.imprint","IMPRINT",FACE,{"disambiguationData":[TD([[makeQuery(id+"F17.imprint","IMPRINT",EDGE,{"derivedFrom":sQuery(id+"F17.wireOp",EDGE,"E118.MirrorC")}),-1.0]])]});
            var Q4;
            Q4=makeQuery(id+"F17.imprint","IMPRINT",FACE,{"disambiguationData":[TD([[makeQuery(id+"F17.imprint","IMPRINT",EDGE,{"derivedFrom":sQuery(id+"F17.wireOp",EDGE,"E120.MirrorC")}),-1.0]])]});
            extrude(context, id + "F18", {"entities" : qUnion([Q0, Q1, Q2, Q3, Q4]), "operationType" : NewBodyOperationType.REMOVE, "oppositeDirection" : true, "depth" : 40 * mm, "offsetDistance" : 25 * mm});
        }
        {
            var Q0;
            Q0=makeQuery(id+"F17.imprint","IMPRINT",FACE,{"disambiguationData":[TD([[makeQuery(id+"F17.imprint","IMPRINT",EDGE,{"derivedFrom":sQuery(id+"F17.wireOp",EDGE,"E115")}),1.0]])]});
            var Q1;
            Q1=makeQuery(id+"F17.imprint","IMPRINT",FACE,{"disambiguationData":[TD([[makeQuery(id+"F17.imprint","IMPRINT",EDGE,{"derivedFrom":sQuery(id+"F17.wireOp",EDGE,"E117")}),1.0]])]});
            var Q2;
            Q2=makeQuery(id+"F17.imprint","IMPRINT",FACE,{"disambiguationData":[TD([[makeQuery(id+"F17.imprint","IMPRINT",EDGE,{"derivedFrom":sQuery(id+"F17.wireOp",EDGE,"E123")}),1.0]])]});
            var Q3;
            Q3=makeQuery(id+"F17.imprint","IMPRINT",FACE,{"disambiguationData":[TD([[makeQuery(id+"F17.imprint","IMPRINT",EDGE,{"derivedFrom":sQuery(id+"F17.wireOp",EDGE,"E119.MirrorC")}),-1.0]])]});
            var Q4;
            Q4=makeQuery(id+"F17.imprint","IMPRINT",FACE,{"disambiguationData":[TD([[makeQuery(id+"F17.imprint","IMPRINT",EDGE,{"derivedFrom":sQuery(id+"F17.wireOp",EDGE,"E121.MirrorC")}),-1.0]])]});
            extrude(context, id + "F19", {"entities" : qUnion([Q0, Q1, Q2, Q3, Q4]), "operationType" : NewBodyOperationType.REMOVE, "oppositeDirection" : true, "depth" : 52 * mm, "offsetDistance" : 25 * mm});
        }
    });
